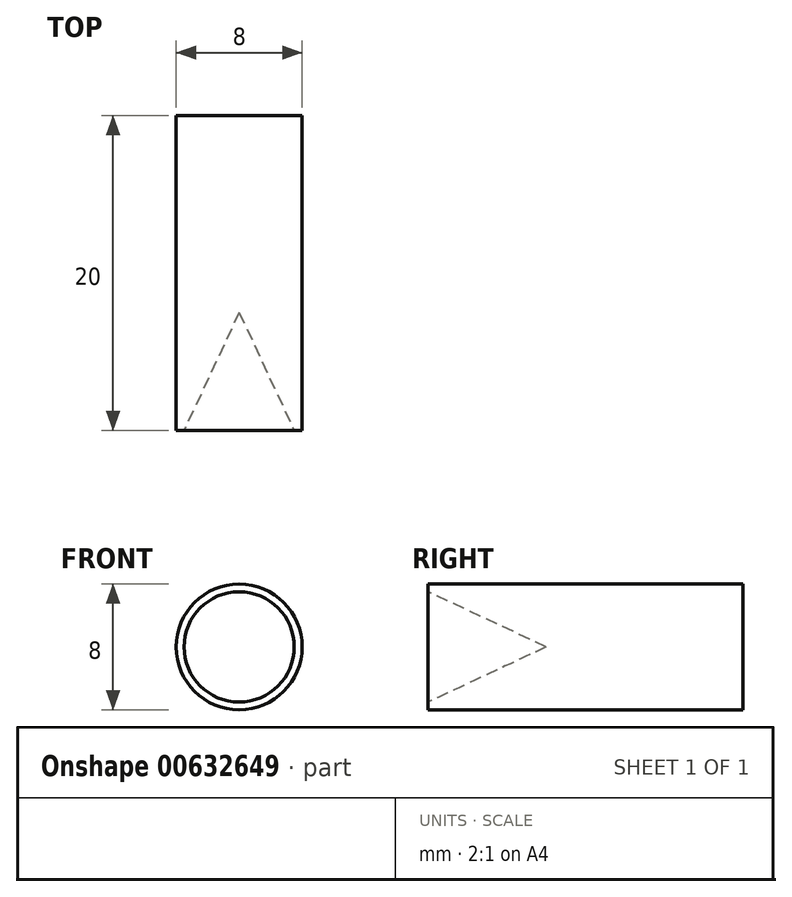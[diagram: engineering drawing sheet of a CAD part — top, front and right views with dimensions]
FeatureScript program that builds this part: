
annotation { "Feature Type Name" : "Feature", "Feature Type Description" : "" }
export const myFeature = defineFeature(function(context is Context, id is Id, definition is map)
    precondition{}
    {
        {
            var Q0;
            Q0=qCreatedBy(makeId("Front.planeOp"),FACE);
            var sketch = newSketch(context, id + "F0", { "sketchPlane" : qUnion([Q0])});
            skCircle(sketch, "E0", {"center": v(0, 0) * mm, "radius": 4 * mm});
            skCircle(sketch, "E1", {"center": v(0, 0) * mm, "radius": 3.5 * mm});
            skSolve(sketch);
        }
        {
            var Q0;
            Q0=makeQuery(id+"F0.imprint","IMPRINT",FACE,{"disambiguationData":[TD([[makeQuery(id+"F0.imprint","IMPRINT",EDGE,{"derivedFrom":sQuery(id+"F0.wireOp",EDGE,"E0")}),1.0]])]});
            var Q1;
            Q1=makeQuery(id+"F0.imprint","IMPRINT",FACE,{"disambiguationData":[TD([[makeQuery(id+"F0.imprint","IMPRINT",EDGE,{"derivedFrom":sQuery(id+"F0.wireOp",EDGE,"E1")}),1.0]])]});
            extrude(context, id + "F1", {"entities" : qUnion([Q0, Q1]), "oppositeDirection" : true, "depth" : 20 * mm, "offsetDistance" : 25 * mm});
        }
        {
            var Q0;
            Q0=qCreatedBy(makeId("Right.planeOp"),FACE);
            var sketch = newSketch(context, id + "F2", { "sketchPlane" : qUnion([Q0])});
            skPoint(sketch, "E2", {"position": v(7.5, 0) * mm});
            skSolve(sketch);
        }
        {
            var Q1;
            Q1=makeQuery(id+"F0.imprint","IMPRINT",FACE,{"disambiguationData":[TD([[makeQuery(id+"F0.imprint","IMPRINT",EDGE,{"derivedFrom":sQuery(id+"F0.wireOp",EDGE,"E1")}),1.0]])]});
            var Q2;
            Q2=sQuery(id+"F2.wireOp",VERTEX,"E2");
            loft(context, id + "F3", {"operationType" : NewBodyOperationType.REMOVE, "sheetProfilesArray" : [{ "sheetProfileEntities" : qUnion([Q1]) }, { "sheetProfileEntities" : qUnion([Q2]) }]});
        }
    });
